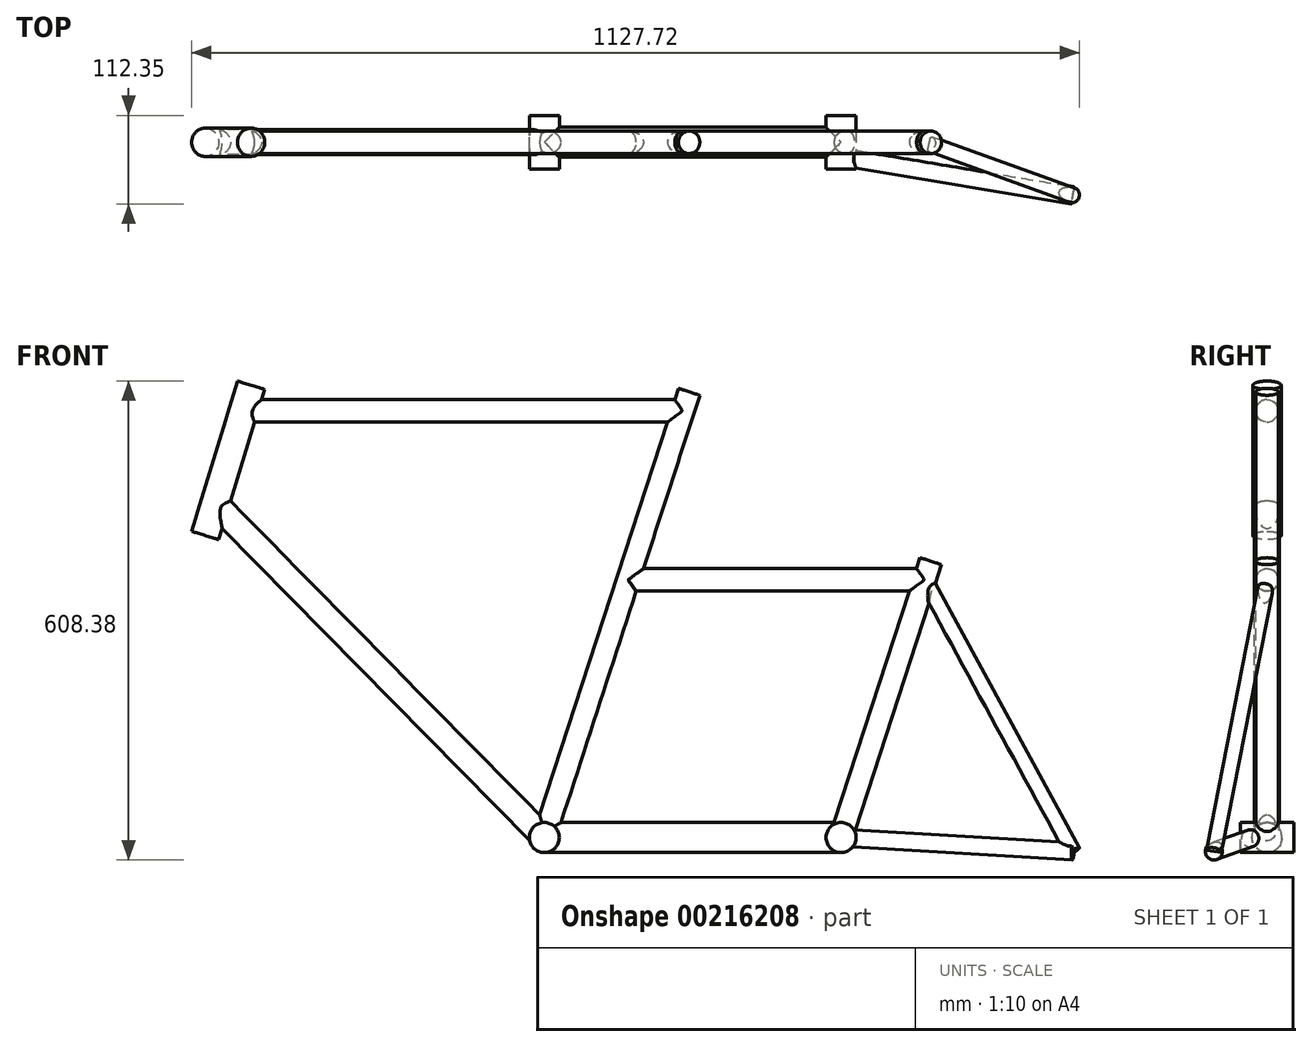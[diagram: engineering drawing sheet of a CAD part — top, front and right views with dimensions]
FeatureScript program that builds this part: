
annotation { "Feature Type Name" : "Feature", "Feature Type Description" : "" }
export const myFeature = defineFeature(function(context is Context, id is Id, definition is map)
    precondition{}
    {
        {
            var Q0;
            Q0=qCreatedBy(makeId("Front.planeOp"),FACE);
            var sketch = newSketch(context, id + "F0", { "sketchPlane" : qUnion([Q0])});
            skLineSegment(sketch, "E0", {"start": v(0, 0) * mm, "end": v(176.14, 542.1) * mm});
            skLineSegment(sketch, "E1", {"start": v(-382.35, 542.09) * mm, "end": v(-527.6, 67) * mm, "construction": true});
            skLineSegment(sketch, "E2.0", {"start": v(1276.12, 67) * mm, "end": v(-807.18, 67) * mm, "construction": true});
            skLineSegment(sketch, "E3", {"start": v(-372.4, 574.65) * mm, "end": v(-430.75, 383.8) * mm});
            skLineSegment(sketch, "E4", {"start": v(0, 0) * mm, "end": v(-418.23, 424.73) * mm});
            skLineSegment(sketch, "E5", {"start": v(483.36, 327.33) * mm, "end": v(377, 0) * mm});
            skLineSegment(sketch, "E6", {"start": v(0, 0) * mm, "end": v(377, 0) * mm});
            skLineSegment(sketch, "E7", {"start": v(798.58, -257.5) * mm, "end": v(-876.38, -257.5) * mm, "construction": true});
            skLineSegment(sketch, "E8", {"start": v(-527.6, 67) * mm, "end": v(-626.81, -257.5) * mm});
            skLineSegment(sketch, "E9", {"start": v(-626.81, -257.5) * mm, "end": v(-586.81, -257.5) * mm});
            skLineSegment(sketch, "E10", {"start": v(-586.81, -257.5) * mm, "end": v(-577.2, 67) * mm});
            skPoint(sketch, "E10.endSnap0", {"position": v(-577.2, -95.25) * mm});
            skCircle(sketch, "E11", {"center": v(-577.2, 67) * mm, "radius": 324.63 * mm});
            skLineSegment(sketch, "E12", {"start": v(-577.2, 67) * mm, "end": v(-531.84, 53.13) * mm});
            skLineSegment(sketch, "E13", {"start": v(377, 0) * mm, "end": v(671.36, -17.5) * mm});
            skLineSegment(sketch, "E14", {"start": v(483.36, 327.33) * mm, "end": v(671.36, -17.5) * mm});
            skLineSegment(sketch, "E15", {"start": v(-382.35, 542.09) * mm, "end": v(176.14, 542.1) * mm});
            skLineSegment(sketch, "E16", {"start": v(483.36, 327.33) * mm, "end": v(106.36, 327.33) * mm});
            skCircle(sketch, "E17", {"center": v(671.36, -17.5) * mm, "radius": 240 * mm});
            skLineSegment(sketch, "E18", {"start": v(671.36, -17.5) * mm, "end": v(-531.84, -17.5) * mm, "construction": true});
            skSolve(sketch);
        }
        {
            var Q0;
            Q0=qCreatedBy(makeId("Front.planeOp"),FACE);
            cPlane(context, id + "F1", {"entities" : qUnion([Q0]), "cplaneType" : CPlaneType.OFFSET, "offset" : 34 * mm, "width" : 152.4 * mm, "height" : 152.4 * mm});
        }
        {
            var Q0;
            Q0=qCreatedBy(id+"F1.planeOp",FACE);
            var sketch = newSketch(context, id + "F2", { "sketchPlane" : qUnion([Q0])});
            skCircle(sketch, "E19", {"center": v(0, 0) * mm, "radius": 19.05 * mm});
            skSolve(sketch);
        }
        {
            var Q0;
            Q0=makeQuery(id+"F2.imprint","IMPRINT",FACE,{"disambiguationData":[TD([[makeQuery(id+"F2.imprint","IMPRINT",EDGE,{"derivedFrom":sQuery(id+"F2.wireOp",EDGE,"E19")}),1.0]])]});
            extrude(context, id + "F3", {"entities" : qUnion([Q0]), "oppositeDirection" : true, "depth" : 68 * mm});
        }
        {
            var Q0;
            Q0=qCreatedBy(makeId("Right.planeOp"),FACE);
            var sketch = newSketch(context, id + "F4", { "sketchPlane" : qUnion([Q0])});
            skCircle(sketch, "E20", {"center": v(0, 0) * mm, "radius": 19.05 * mm});
            skSolve(sketch);
        }
        {
            var Q0;
            Q0=qCreatedBy(id+"F1.planeOp",FACE);
            var sketch = newSketch(context, id + "F5", { "sketchPlane" : qUnion([Q0])});
            skCircle(sketch, "E21", {"center": v(377, 0) * mm, "radius": 19.05 * mm});
            skSolve(sketch);
        }
        {
            var Q0;
            Q0=makeQuery(id+"F5.imprint","IMPRINT",FACE,{"disambiguationData":[TD([[makeQuery(id+"F5.imprint","IMPRINT",EDGE,{"derivedFrom":sQuery(id+"F5.wireOp",EDGE,"E21")}),1.0]])]});
            var Q1;
            Q1=sQuery(id+"F5.wireOp",EDGE,"E21");
            extrude(context, id + "F6", {"entities" : qUnion([Q0]), "operationType" : NewBodyOperationType.ADD, "surfaceEntities" : qUnion([Q1]), "oppositeDirection" : true, "depth" : 68 * mm});
        }
        {
            var Q0;
            Q0=makeQuery(id+"F4.imprint","IMPRINT",FACE,{"disambiguationData":[TD([[makeQuery(id+"F4.imprint","IMPRINT",EDGE,{"derivedFrom":sQuery(id+"F4.wireOp",EDGE,"E20")}),1.0]])]});
            var Q1;
            Q1=makeQuery(id+"F6.opExtrude","SWEPT_FACE",FACE,{"disambiguationData":[OSD([sQuery(id+"F5.wireOp",EDGE,"E21")])]});
            var Q2;
            Q2=makeQuery(id+"Fevw2kgL0nShUnP_1.opExtrude","SWEPT_BODY",BODY,{"disambiguationData":[OSD([sQuery(id+"F5.wireOp",EDGE,"E21")])]});
            extrude(context, id + "F7", {"entities" : qUnion([Q0]), "operationType" : NewBodyOperationType.ADD, "endBound" : BoundingType.UP_TO_SURFACE, "endBoundEntityFace" : qUnion([Q1]), "endBoundEntityBody" : qUnion([Q2]), "depth" : 154 * mm});
        }
        {
            var Q0;
            Q0=sQuery(id+"F0.wireOp",EDGE,"E0");
            var Q1;
            Q1=sQuery(id+"F0.wireOp",VERTEX,"E0.end");
            cPlane(context, id + "F8", {"entities" : qUnion([Q0, Q1]), "cplaneType" : CPlaneType.LINE_POINT, "offset" : 152.4 * mm, "width" : 152.4 * mm, "height" : 152.4 * mm});
        }
        {
            var Q0;
            Q0=qCreatedBy(id+"F8.planeOp",FACE);
            var sketch = newSketch(context, id + "F9", { "sketchPlane" : qUnion([Q0])});
            skCircle(sketch, "E22", {"center": v(0, 0) * mm, "radius": 14.3 * mm});
            skSolve(sketch);
        }
        {
            var Q0;
            Q0=makeQuery(id+"F9.imprint","IMPRINT",FACE,{"disambiguationData":[TD([[makeQuery(id+"F9.imprint","IMPRINT",EDGE,{"derivedFrom":sQuery(id+"F9.wireOp",EDGE,"E22")}),1.0]])]});
            var Q1;
            Q1=makeQuery(id+"F3.opExtrude","SWEPT_BODY",BODY,{"disambiguationData":[OSD([sQuery(id+"F2.wireOp",EDGE,"E19")])]});
            extrude(context, id + "F10", {"entities" : qUnion([Q0]), "operationType" : NewBodyOperationType.ADD, "endBound" : BoundingType.UP_TO_BODY, "oppositeDirection" : true, "endBoundEntityBody" : qUnion([Q1]), "depth" : 25.4 * mm, "hasSecondDirection" : true, "secondDirectionOppositeDirection" : false, "secondDirectionDepth" : 25.4 * mm});
        }
        {
            var Q0;
            Q0=sQuery(id+"F0.wireOp",EDGE,"E13");
            cPlane(context, id + "F11", {"entities" : qUnion([Q0]), "cplaneType" : CPlaneType.LINE_ANGLE, "offset" : 152.4 * mm, "angle" : 90 * degree, "width" : 152.4 * mm, "height" : 152.4 * mm});
        }
        {
            var Q0;
            Q0=sQuery(id+"F0.wireOp",EDGE,"E5");
            var Q1;
            Q1=sQuery(id+"F0.wireOp",VERTEX,"E14.start");
            cPlane(context, id + "F12", {"entities" : qUnion([Q0, Q1]), "cplaneType" : CPlaneType.LINE_POINT, "offset" : 152.4 * mm, "width" : 152.4 * mm, "height" : 152.4 * mm});
        }
        {
            var Q0;
            Q0=qCreatedBy(id+"F12.planeOp",FACE);
            var sketch = newSketch(context, id + "F13", { "sketchPlane" : qUnion([Q0])});
            skCircle(sketch, "E23", {"center": v(358.55, 0) * mm, "radius": 14.3 * mm});
            skSolve(sketch);
        }
        {
            var Q0;
            Q0=sQuery(id+"F0.wireOp",EDGE,"E4");
            var Q1;
            Q1=sQuery(id+"F0.wireOp",VERTEX,"E4.end");
            cPlane(context, id + "F14", {"entities" : qUnion([Q0, Q1]), "cplaneType" : CPlaneType.LINE_POINT, "offset" : 152.4 * mm, "width" : 152.4 * mm, "height" : 152.4 * mm});
        }
        {
            var Q0;
            Q0=qCreatedBy(id+"F14.planeOp",FACE);
            var sketch = newSketch(context, id + "F15", { "sketchPlane" : qUnion([Q0])});
            skCircle(sketch, "E24", {"center": v(0, 0) * mm, "radius": 15.9 * mm});
            skSolve(sketch);
        }
        {
            var Q0;
            Q0=makeQuery(id+"F15.imprint","IMPRINT",FACE,{"disambiguationData":[TD([[makeQuery(id+"F15.imprint","IMPRINT",EDGE,{"derivedFrom":sQuery(id+"F15.wireOp",EDGE,"E24")}),1.0]])]});
            var Q1;
            Q1=makeQuery(id+"F3.opExtrude","SWEPT_BODY",BODY,{"disambiguationData":[OSD([sQuery(id+"F2.wireOp",EDGE,"E19")])]});
            extrude(context, id + "F16", {"entities" : qUnion([Q0]), "operationType" : NewBodyOperationType.ADD, "endBound" : BoundingType.UP_TO_BODY, "oppositeDirection" : true, "endBoundEntityBody" : qUnion([Q1]), "depth" : 25.4 * mm});
        }
        {
            var Q0;
            Q0=sQuery(id+"F0.wireOp",EDGE,"E3");
            var Q1;
            Q1=sQuery(id+"F0.wireOp",VERTEX,"E3.start");
            cPlane(context, id + "F17", {"entities" : qUnion([Q0, Q1]), "cplaneType" : CPlaneType.LINE_POINT, "offset" : 152.4 * mm, "width" : 152.4 * mm, "height" : 152.4 * mm});
        }
        {
            var Q0;
            Q0=qCreatedBy(id+"F17.planeOp",FACE);
            var sketch = newSketch(context, id + "F18", { "sketchPlane" : qUnion([Q0])});
            skCircle(sketch, "E25", {"center": v(-524.14, 0) * mm, "radius": 18 * mm});
            skSolve(sketch);
        }
        {
            var Q0;
            Q0=sQuery(id+"F0.wireOp",EDGE,"E14");
            cPlane(context, id + "F19", {"entities" : qUnion([Q0]), "cplaneType" : CPlaneType.LINE_ANGLE, "offset" : 152.4 * mm, "angle" : 0 * degree, "width" : 152.4 * mm, "height" : 152.4 * mm});
        }
        {
            var Q0;
            Q0=makeQuery(id+"F18.imprint","IMPRINT",FACE,{"disambiguationData":[TD([[makeQuery(id+"F18.imprint","IMPRINT",EDGE,{"derivedFrom":sQuery(id+"F18.wireOp",EDGE,"E25")}),1.0]])]});
            var Q1;
            Q1=sQuery(id+"F18.wireOp",EDGE,"E25");
            var Q2;
            Q2=sQuery(id+"F0.wireOp",VERTEX,"E3.end");
            extrude(context, id + "F20", {"entities" : qUnion([Q0]), "operationType" : NewBodyOperationType.ADD, "surfaceEntities" : qUnion([Q1]), "endBound" : BoundingType.UP_TO_VERTEX, "endBoundEntityVertex" : qUnion([Q2]), "depth" : 199 * mm});
        }
        {
            var Q0;
            Q0=sQuery(id+"F0.wireOp",VERTEX,"E15.start");
            var Q1;
            Q1=sQuery(id+"F0.wireOp",EDGE,"E15");
            cPlane(context, id + "F21", {"entities" : qUnion([Q0, Q1]), "cplaneType" : CPlaneType.LINE_POINT, "offset" : 25 * mm, "width" : 150 * mm, "height" : 150 * mm});
        }
        {
            var Q0;
            Q0=qCreatedBy(id+"F21.planeOp",FACE);
            var sketch = newSketch(context, id + "F22", { "sketchPlane" : qUnion([Q0])});
            skCircle(sketch, "E26", {"center": v(0, 542.1) * mm, "radius": 14.29 * mm});
            skSolve(sketch);
        }
        {
            var Q0;
            Q0=qSketchRegion(id+"F22",true);
            var Q1;
            Q1=makeQuery(id+"F10.opExtrude","SWEPT_FACE",FACE,{"disambiguationData":[OSD([sQuery(id+"F9.wireOp",EDGE,"E22")])]});
            var Q2;
            Q2=makeQuery(id+"F3.opExtrude","SWEPT_BODY",BODY,{"disambiguationData":[OSD([sQuery(id+"F2.wireOp",EDGE,"E19")])]});
            extrude(context, id + "F23", {"entities" : qUnion([Q0]), "operationType" : NewBodyOperationType.ADD, "endBound" : BoundingType.UP_TO_SURFACE, "endBoundEntityFace" : qUnion([Q1]), "endBoundEntityBody" : qUnion([Q2]), "depth" : 25 * mm});
        }
        {
            var Q0;
            Q0=sQuery(id+"F0.wireOp",EDGE,"E16");
            var Q1;
            Q1=sQuery(id+"F0.wireOp",VERTEX,"E16.end");
            cPlane(context, id + "F24", {"entities" : qUnion([Q0, Q1]), "cplaneType" : CPlaneType.LINE_POINT, "offset" : 25 * mm, "width" : 150 * mm, "height" : 150 * mm});
        }
        {
            var Q0;
            Q0=makeQuery(id+"F13.imprint","IMPRINT",FACE,{"disambiguationData":[TD([[makeQuery(id+"F13.imprint","IMPRINT",EDGE,{"derivedFrom":sQuery(id+"F13.wireOp",EDGE,"E23")}),1.0]])]});
            var Q1;
            Q1=sQuery(id+"F13.wireOp",EDGE,"E23");
            var Q2;
            Q2=makeQuery(id+"F6.opExtrude","SWEPT_FACE",FACE,{"disambiguationData":[OSD([sQuery(id+"F5.wireOp",EDGE,"E21")])]});
            extrude(context, id + "F25", {"entities" : qUnion([Q0]), "operationType" : NewBodyOperationType.ADD, "surfaceEntities" : qUnion([Q1]), "endBound" : BoundingType.UP_TO_SURFACE, "endBoundEntityFace" : qUnion([Q2]), "depth" : 25 * mm, "hasSecondDirection" : true, "secondDirectionOppositeDirection" : true, "secondDirectionDepth" : 25 * mm});
        }
        {
            var Q0;
            Q0=qCreatedBy(id+"F24.planeOp",FACE);
            var sketch = newSketch(context, id + "F26", { "sketchPlane" : qUnion([Q0])});
            skCircle(sketch, "E27", {"center": v(0, 327.33) * mm, "radius": 14.29 * mm});
            skSolve(sketch);
        }
        {
            var Q0;
            Q0 = qSketchRegion(id + "F26", true);
            var Q1;
            Q1=sQuery(id+"F26.wireOp",EDGE,"E27");
            var Q2;
            Q2=makeQuery(id+"F25.opExtrude","SWEPT_FACE",FACE,{"disambiguationData":[OSD([sQuery(id+"F13.wireOp",EDGE,"E23")])]});
            extrude(context, id + "F27", {"entities" : qUnion([Q0]), "operationType" : NewBodyOperationType.ADD, "surfaceEntities" : qUnion([Q1]), "endBound" : BoundingType.UP_TO_SURFACE, "oppositeDirection" : true, "endBoundEntityFace" : qUnion([Q2]), "depth" : 25 * mm});
        }
        {
            var Q0;
            Q0=qCreatedBy(id+"F11.planeOp",FACE);
            var sketch = newSketch(context, id + "F28", { "sketchPlane" : qUnion([Q0])});
            skLineSegment(sketch, "E28", {"start": v(671.21, 0) * mm, "end": v(671.21, -67.5) * mm, "construction": true});
            skLineSegment(sketch, "E29", {"start": v(371.57, 0) * mm, "end": v(371.57, -33.53) * mm, "construction": true});
            skLineSegment(sketch, "E30", {"start": v(671.21, -67.5) * mm, "end": v(371.57, -17.65) * mm});
            skSolve(sketch);
        }
        {
            var Q0;
            Q0=sQuery(id+"F28.wireOp",EDGE,"E30");
            var Q1;
            Q1=sQuery(id+"F28.wireOp",VERTEX,"E28.end");
            cPlane(context, id + "F29", {"entities" : qUnion([Q0, Q1]), "cplaneType" : CPlaneType.LINE_POINT, "offset" : 25 * mm, "width" : 150 * mm, "height" : 150 * mm});
        }
        {
            var Q0;
            Q0=qCreatedBy(id+"F29.planeOp",FACE);
            var sketch = newSketch(context, id + "F30", { "sketchPlane" : qUnion([Q0])});
            skCircle(sketch, "E31", {"center": v(-43.56, 22.36) * mm, "radius": 11 * mm});
            skSolve(sketch);
        }
        {
            var Q0;
            Q0=makeQuery(id+"F30.imprint","IMPRINT",FACE,{"disambiguationData":[TD([[makeQuery(id+"F30.imprint","IMPRINT",EDGE,{"derivedFrom":sQuery(id+"F30.wireOp",EDGE,"E31")}),1.0]])]});
            var Q1;
            Q1=sQuery(id+"F30.wireOp",EDGE,"E31");
            var Q2;
            Q2=makeQuery(id+"F6.opExtrude","SWEPT_FACE",FACE,{"disambiguationData":[OSD([sQuery(id+"F5.wireOp",EDGE,"E21")])]});
            extrude(context, id + "F31", {"entities" : qUnion([Q0]), "operationType" : NewBodyOperationType.ADD, "surfaceEntities" : qUnion([Q1]), "endBound" : BoundingType.UP_TO_SURFACE, "endBoundEntityFace" : qUnion([Q2]), "depth" : 25 * mm});
        }
        {
            var Q0;
            Q0=qCreatedBy(id+"F19.planeOp",FACE);
            var sketch = newSketch(context, id + "F32", { "sketchPlane" : qUnion([Q0])});
            skLineSegment(sketch, "E32", {"start": v(0, 56.02) * mm, "end": v(67.5, -336.72) * mm});
            skSolve(sketch);
        }
        {
            var Q0;
            Q0=sQuery(id+"F32.wireOp",VERTEX,"E32.end");
            var Q1;
            Q1=sQuery(id+"F32.wireOp",EDGE,"E32");
            cPlane(context, id + "F33", {"entities" : qUnion([Q0, Q1]), "cplaneType" : CPlaneType.LINE_POINT, "offset" : 25 * mm, "width" : 150 * mm, "height" : 150 * mm});
        }
        {
            var Q0;
            Q0=qCreatedBy(id+"F33.planeOp",FACE);
            var sketch = newSketch(context, id + "F34", { "sketchPlane" : qUnion([Q0])});
            skCircle(sketch, "E33", {"center": v(577.74, 62.88) * mm, "radius": 9.53 * mm});
            skSolve(sketch);
        }
        {
            var Q0;
            Q0=makeQuery(id+"F34.imprint","IMPRINT",FACE,{"disambiguationData":[TD([[makeQuery(id+"F34.imprint","IMPRINT",EDGE,{"derivedFrom":sQuery(id+"F34.wireOp",EDGE,"E33")}),1.0]])]});
            var Q1;
            Q1=makeQuery(id+"F25.opExtrude","SWEPT_FACE",FACE,{"disambiguationData":[OSD([sQuery(id+"F13.wireOp",EDGE,"E23")])]});
            extrude(context, id + "F35", {"entities" : qUnion([Q0]), "operationType" : NewBodyOperationType.ADD, "endBound" : BoundingType.UP_TO_SURFACE, "oppositeDirection" : true, "endBoundEntityFace" : qUnion([Q1]), "depth" : 25 * mm});
        }
        {
            var Q0;
            Q0=qCreatedBy(id+"F11.planeOp",FACE);
            var sketch = newSketch(context, id + "F36", { "sketchPlane" : qUnion([Q0])});
            skCircle(sketch, "E34", {"center": v(449.12, 0) * mm, "radius": 17.5 * mm});
            skSolve(sketch);
        }
    });
